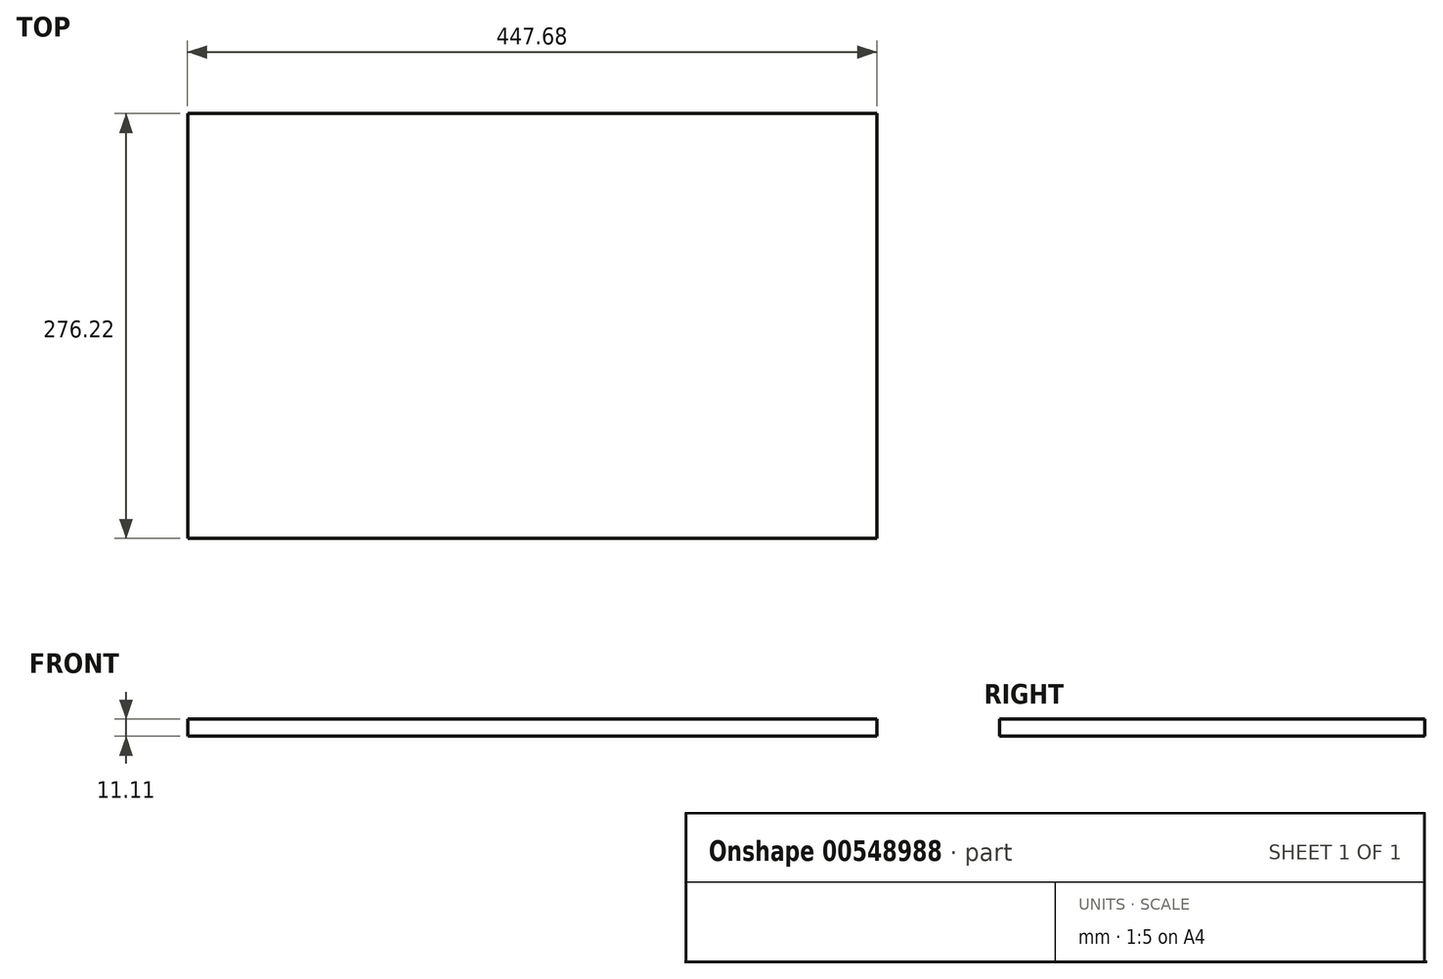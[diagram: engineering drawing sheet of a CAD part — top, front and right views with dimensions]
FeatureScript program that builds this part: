
annotation { "Feature Type Name" : "Feature", "Feature Type Description" : "" }
export const myFeature = defineFeature(function(context is Context, id is Id, definition is map)
    precondition{}
    {
        {
            var Q0;
            Q0=qCreatedBy(makeId("Top.planeOp"),FACE);
            var sketch = newSketch(context, id + "F0", { "sketchPlane" : qUnion([Q0])});
            skLineSegment(sketch, "E0.bottom", {"start": v(223.84, -138.11) * mm, "end": v(-223.84, -138.11) * mm});
            skLineSegment(sketch, "E0.top", {"start": v(223.84, 138.11) * mm, "end": v(-223.84, 138.11) * mm});
            skLineSegment(sketch, "E0.left", {"start": v(223.84, -138.11) * mm, "end": v(223.84, 138.11) * mm});
            skLineSegment(sketch, "E0.right", {"start": v(-223.84, -138.11) * mm, "end": v(-223.84, 138.11) * mm});
            skPoint(sketch, "E0.middle", {"position": v(0, 0) * mm});
            skSolve(sketch);
        }
        {
            var Q0;
            Q0 = qSketchRegion(id + "F0", true);
            extrude(context, id + "F1", {"entities" : qUnion([Q0]), "depth" : 11.1 * mm, "offsetDistance" : 25.4 * mm});
        }
    });
